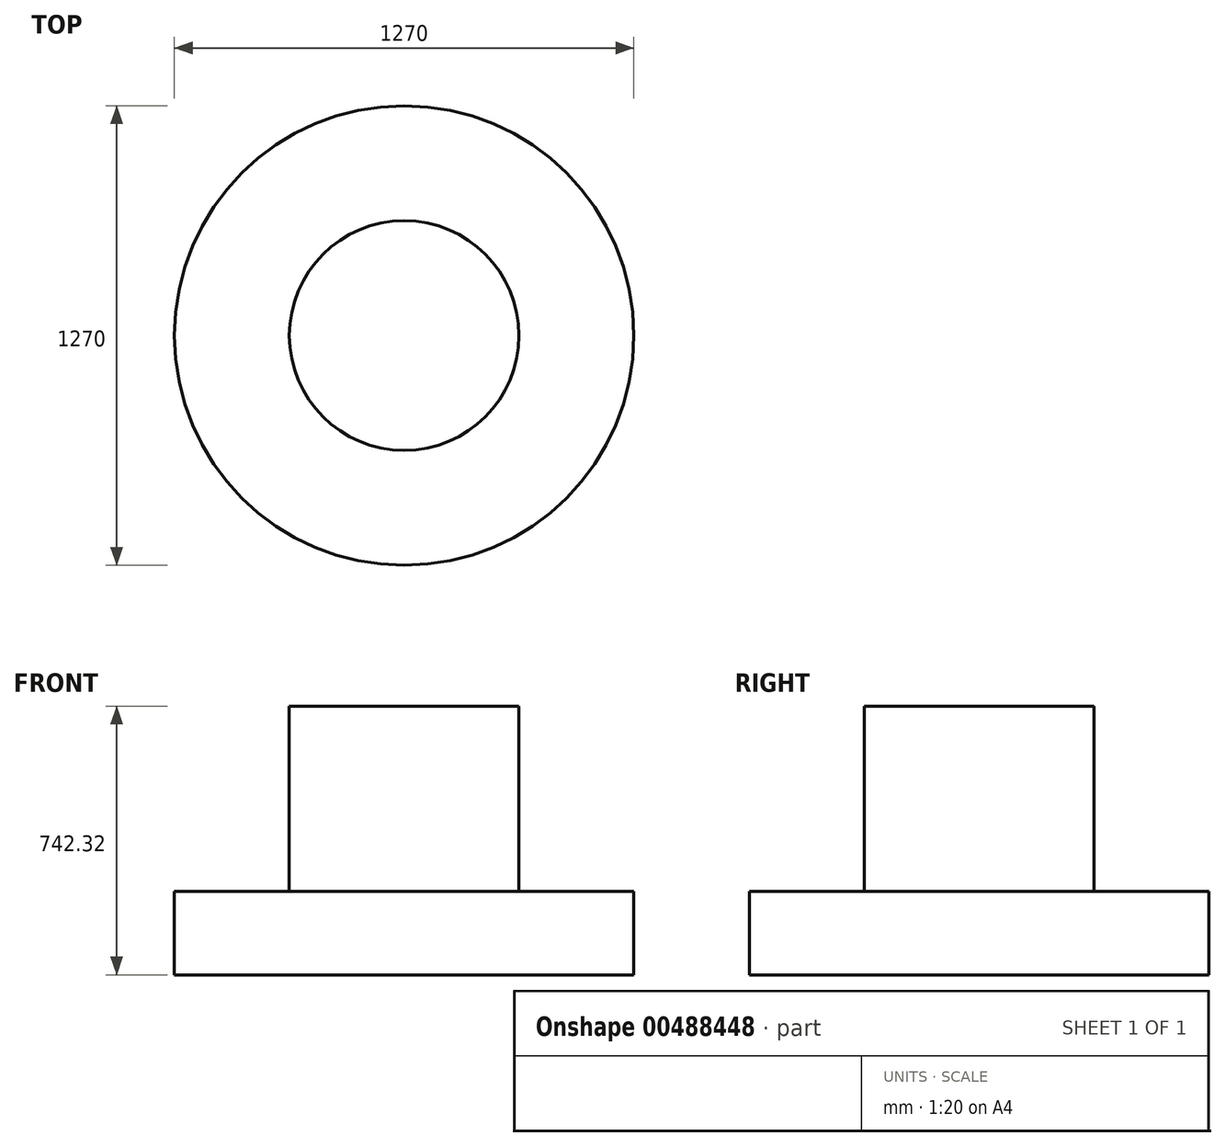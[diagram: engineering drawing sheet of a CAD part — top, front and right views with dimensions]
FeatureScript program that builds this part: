
annotation { "Feature Type Name" : "Feature", "Feature Type Description" : "" }
export const myFeature = defineFeature(function(context is Context, id is Id, definition is map)
    precondition{}
    {
        {
            var Q0;
            Q0=qCreatedBy(makeId("Top.planeOp"),FACE);
            var sketch = newSketch(context, id + "F0", { "sketchPlane" : qUnion([Q0])});
            skCircle(sketch, "E0", {"center": v(0, 0) * mm, "radius": 635 * mm});
            skSolve(sketch);
        }
        {
            var Q0;
            Q0 = qSketchRegion(id + "F0", true);
            extrude(context, id + "F1", {"entities" : qUnion([Q0]), "depth" : 230.64 * mm});
        }
        {
            var Q0;
            Q0=makeQuery(id+"F1.opExtrude","CAP_FACE",FACE,{"disambiguationData":[OSD([sQuery(id+"F0.wireOp",EDGE,"E0")])],"isStart":false});
            var sketch = newSketch(context, id + "F2", { "sketchPlane" : qUnion([Q0])});
            skCircle(sketch, "E1", {"center": v(0, 0) * mm, "radius": 317.5 * mm});
            skSolve(sketch);
        }
        {
            var Q0;
            Q0 = qSketchRegion(id + "F2", true);
            var Q1;
            Q1=sQuery(id+"F2.wireOp",EDGE,"E1");
            extrude(context, id + "F3", {"bodyType" : ToolBodyType.SURFACE, "operationType" : NewBodyOperationType.ADD, "surfaceEntities" : qUnion([Q0, Q1]), "depth" : 511.68 * mm});
        }
    });
